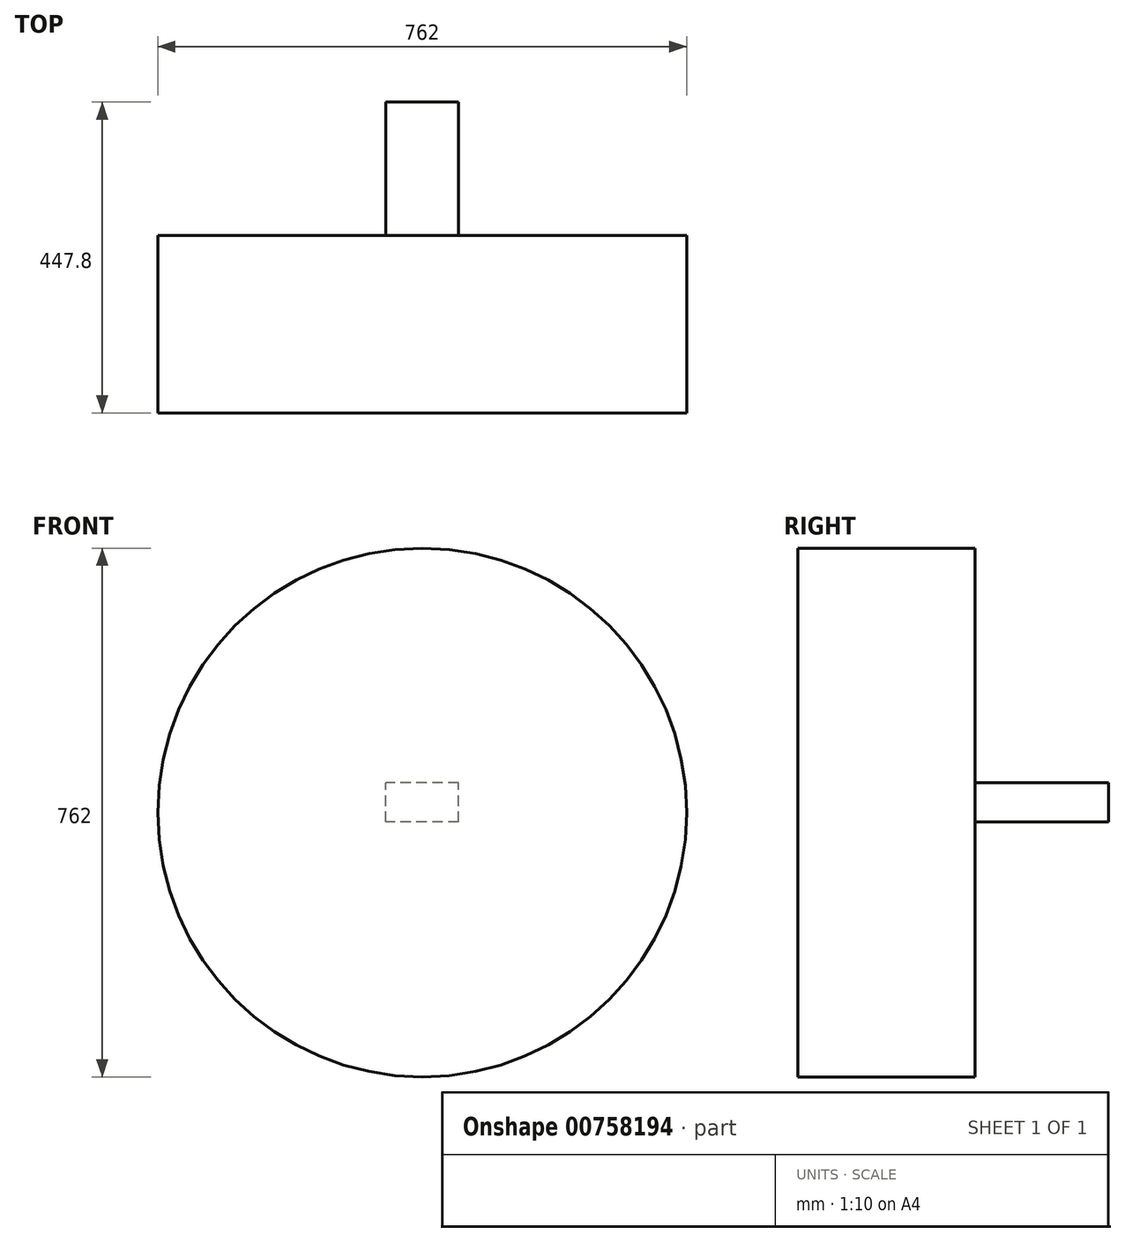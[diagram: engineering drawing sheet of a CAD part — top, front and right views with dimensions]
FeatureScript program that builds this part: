
annotation { "Feature Type Name" : "Feature", "Feature Type Description" : "" }
export const myFeature = defineFeature(function(context is Context, id is Id, definition is map)
    precondition{}
    {
        {
            var Q0;
            Q0=qCreatedBy(makeId("Front.planeOp"),FACE);
            var sketch = newSketch(context, id + "F0", { "sketchPlane" : qUnion([Q0])});
            skLineSegment(sketch, "E0.bottom", {"start": v(52.58, -28.35) * mm, "end": v(-52.58, -28.35) * mm});
            skLineSegment(sketch, "E0.top", {"start": v(52.58, 28.35) * mm, "end": v(-52.58, 28.35) * mm});
            skLineSegment(sketch, "E0.left", {"start": v(52.58, -28.35) * mm, "end": v(52.58, 28.35) * mm});
            skLineSegment(sketch, "E0.right", {"start": v(-52.58, -28.35) * mm, "end": v(-52.58, 28.35) * mm});
            skPoint(sketch, "E0.middle", {"position": v(0, 0) * mm});
            skSolve(sketch);
        }
        {
            var Q0;
            Q0=makeQuery(id+"F0.imprint","IMPRINT",FACE,{"disambiguationData":[TD([[makeQuery(id+"F0.imprint","IMPRINT",EDGE,{"derivedFrom":sQuery(id+"F0.wireOp",EDGE,"E0.bottom")}),-1.0]])]});
            extrude(context, id + "F1", {"entities" : qUnion([Q0]), "oppositeDirection" : true, "depth" : 192.02 * mm, "offsetDistance" : 25.4 * mm});
        }
        {
            var Q0;
            Q0=qCreatedBy(makeId("Front.planeOp"),FACE);
            var sketch = newSketch(context, id + "F2", { "sketchPlane" : qUnion([Q0])});
            skCircle(sketch, "E1", {"center": v(0, -14.88) * mm, "radius": 381 * mm});
            skSolve(sketch);
        }
        {
            var Q0;
            Q0=makeQuery(id+"F2.imprint","IMPRINT",FACE,{"disambiguationData":[TD([[makeQuery(id+"F2.imprint","IMPRINT",EDGE,{"derivedFrom":sQuery(id+"F2.wireOp",EDGE,"E1")}),1.0]])]});
            extrude(context, id + "F3", {"entities" : qUnion([Q0]), "operationType" : NewBodyOperationType.ADD, "depth" : 255.78 * mm, "offsetDistance" : 25.4 * mm});
        }
    });
